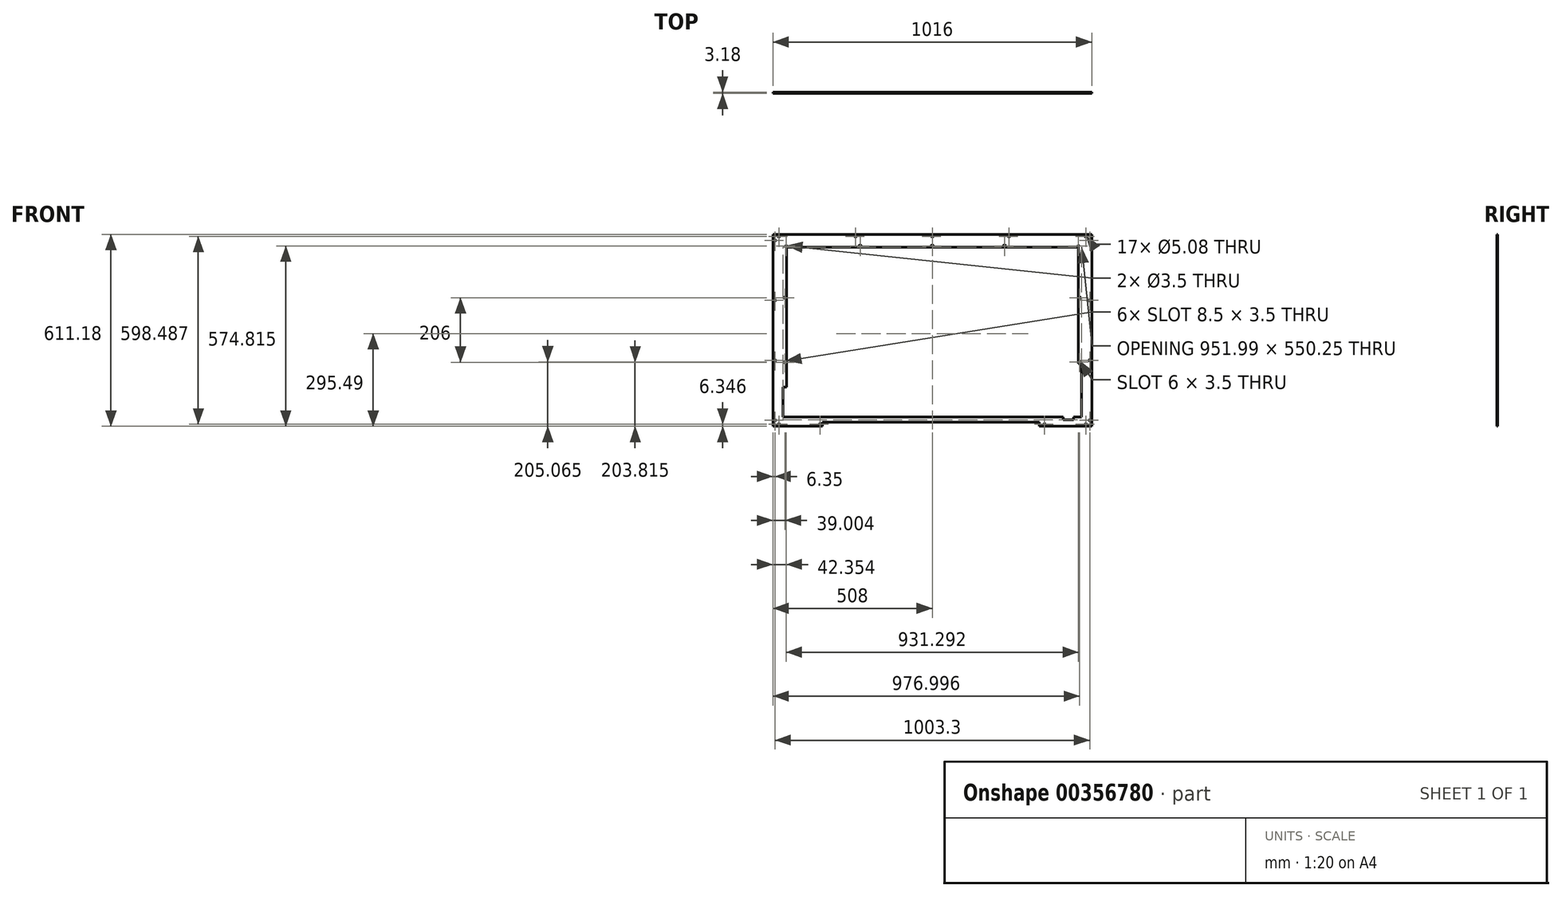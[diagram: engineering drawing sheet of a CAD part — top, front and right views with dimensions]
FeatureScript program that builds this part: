
annotation { "Feature Type Name" : "Feature", "Feature Type Description" : "" }
export const myFeature = defineFeature(function(context is Context, id is Id, definition is map)
    precondition{}
    {
        {
            var Q0;
            Q0=qCreatedBy(makeId("Front.planeOp"),FACE);
            var sketch = newSketch(context, id + "F0", { "sketchPlane" : qUnion([Q0])});
            skLineSegment(sketch, "E0.bottom", {"start": v(495.3, 292.9) * mm, "end": v(-495.3, 292.9) * mm});
            skLineSegment(sketch, "E0.top", {"start": v(495.3, -292.9) * mm, "end": v(-495.3, -292.9) * mm});
            skLineSegment(sketch, "E0.left", {"start": v(495.3, 292.9) * mm, "end": v(495.3, -292.9) * mm});
            skLineSegment(sketch, "E0.right", {"start": v(-495.3, 292.9) * mm, "end": v(-495.3, -292.9) * mm});
            skPoint(sketch, "E0.middle", {"position": v(0, 0) * mm});
            skLineSegment(sketch, "E1.0", {"start": v(-508, 305.6) * mm, "end": v(-508, -305.6) * mm});
            skLineSegment(sketch, "E1.1", {"start": v(508, 305.6) * mm, "end": v(-508, 305.6) * mm});
            skLineSegment(sketch, "E1.2", {"start": v(508, 305.6) * mm, "end": v(508, -305.6) * mm});
            skLineSegment(sketch, "E1.3", {"start": v(508, -305.6) * mm, "end": v(-508, -305.6) * mm});
            skLineSegment(sketch, "E2.bottom", {"start": v(-476, 276.23) * mm, "end": v(476, 276.23) * mm});
            skLineSegment(sketch, "E2.top", {"start": v(-476, -276.23) * mm, "end": v(476, -276.23) * mm});
            skLineSegment(sketch, "E2.left", {"start": v(-476, 276.23) * mm, "end": v(-476, -276.23) * mm});
            skLineSegment(sketch, "E2.right", {"start": v(476, 276.22) * mm, "end": v(476, -276.23) * mm});
            skLineSegment(sketch, "E3", {"start": v(-508, 305.6) * mm, "end": v(-495.3, 292.9) * mm});
            skPoint(sketch, "E4.middle", {"position": v(-501.65, 299.24) * mm});
            skLineSegment(sketch, "E5.bottom", {"start": v(-355.3, -296.7) * mm, "end": v(-360.38, -296.7) * mm});
            skLineSegment(sketch, "E5.top", {"start": v(-355.3, -301.78) * mm, "end": v(-360.38, -301.78) * mm});
            skLineSegment(sketch, "E5.left", {"start": v(-355.3, -296.7) * mm, "end": v(-355.3, -301.78) * mm});
            skLineSegment(sketch, "E5.right", {"start": v(-360.38, -296.7) * mm, "end": v(-360.38, -301.78) * mm});
            skPoint(sketch, "E5.middle", {"position": v(-357.84, -299.24) * mm});
            skLineSegment(sketch, "E6.MirrorCS", {"start": v(360.38, -296.7) * mm, "end": v(360.38, -301.78) * mm});
            skLineSegment(sketch, "E7.MirrorCS", {"start": v(355.3, -296.7) * mm, "end": v(360.38, -296.7) * mm});
            skLineSegment(sketch, "E8.MirrorCS", {"start": v(355.3, -296.7) * mm, "end": v(355.3, -301.78) * mm});
            skLineSegment(sketch, "E9.MirrorCS", {"start": v(355.3, -301.78) * mm, "end": v(360.38, -301.78) * mm});
            skLineSegment(sketch, "E10.bottom", {"start": v(-486.41, 296.7) * mm, "end": v(-491.5, 296.7) * mm});
            skLineSegment(sketch, "E10.top", {"start": v(-486.41, 301.78) * mm, "end": v(-491.5, 301.78) * mm});
            skLineSegment(sketch, "E10.left", {"start": v(-486.41, 296.7) * mm, "end": v(-486.41, 301.78) * mm});
            skLineSegment(sketch, "E10.right", {"start": v(-491.5, 296.7) * mm, "end": v(-491.5, 301.78) * mm});
            skPoint(sketch, "E10.middle", {"position": v(-488.95, 299.24) * mm});
            skLineSegment(sketch, "E11.MirrorCS", {"start": v(-504.19, 284) * mm, "end": v(-504.19, 289.08) * mm});
            skLineSegment(sketch, "E12.MirrorCS", {"start": v(-499.11, 289.08) * mm, "end": v(-504.2, 289.08) * mm});
            skLineSegment(sketch, "E13.MirrorCS", {"start": v(-499.11, 284) * mm, "end": v(-499.11, 289.08) * mm});
            skLineSegment(sketch, "E14.MirrorCS", {"start": v(-499.11, 284) * mm, "end": v(-504.2, 284) * mm});
            skCircle(sketch, "E15", {"center": v(-488.95, 299.24) * mm, "radius": 5.97 * mm});
            skLineSegment(sketch, "E16.MirrorCS", {"start": v(499.11, 284) * mm, "end": v(499.11, 289.08) * mm});
            skLineSegment(sketch, "E17.MirrorCS", {"start": v(499.11, 284) * mm, "end": v(504.2, 284) * mm});
            skLineSegment(sketch, "E18.MirrorCS", {"start": v(499.11, 289.08) * mm, "end": v(504.2, 289.08) * mm});
            skLineSegment(sketch, "E19.MirrorCS", {"start": v(504.19, 284) * mm, "end": v(504.19, 289.08) * mm});
            skLineSegment(sketch, "E20.MirrorCS", {"start": v(486.41, 301.78) * mm, "end": v(491.5, 301.78) * mm});
            skLineSegment(sketch, "E21.MirrorCS", {"start": v(486.41, 296.7) * mm, "end": v(486.41, 301.78) * mm});
            skLineSegment(sketch, "E22.MirrorCS", {"start": v(486.41, 296.7) * mm, "end": v(491.5, 296.7) * mm});
            skLineSegment(sketch, "E23.MirrorCS", {"start": v(491.5, 296.7) * mm, "end": v(491.5, 301.78) * mm});
            skPoint(sketch, "E24.MirrorP", {"position": v(488.95, 299.24) * mm});
            skLineSegment(sketch, "E25.MirrorCS", {"start": v(-499.11, -289.08) * mm, "end": v(-504.2, -289.08) * mm});
            skLineSegment(sketch, "E26.MirrorCS", {"start": v(-499.11, -284) * mm, "end": v(-499.11, -289.08) * mm});
            skLineSegment(sketch, "E27.MirrorCS", {"start": v(-499.11, -284) * mm, "end": v(-504.2, -284) * mm});
            skLineSegment(sketch, "E28.MirrorCS", {"start": v(-504.19, -284) * mm, "end": v(-504.19, -289.08) * mm});
            skLineSegment(sketch, "E29.MirrorCS", {"start": v(-486.41, -301.78) * mm, "end": v(-491.5, -301.78) * mm});
            skLineSegment(sketch, "E30.MirrorCS", {"start": v(-491.5, -296.7) * mm, "end": v(-491.5, -301.78) * mm});
            skPoint(sketch, "E31.MirrorP", {"position": v(-488.95, -299.24) * mm});
            skLineSegment(sketch, "E32.MirrorCS", {"start": v(-486.41, -296.7) * mm, "end": v(-486.41, -301.78) * mm});
            skLineSegment(sketch, "E33.MirrorCS", {"start": v(-486.41, -296.7) * mm, "end": v(-491.5, -296.7) * mm});
            skLineSegment(sketch, "E34.MirrorCS", {"start": v(486.41, -296.7) * mm, "end": v(486.41, -301.78) * mm});
            skPoint(sketch, "E35.MirrorP", {"position": v(488.95, -299.24) * mm});
            skLineSegment(sketch, "E36.MirrorCS", {"start": v(491.5, -296.7) * mm, "end": v(491.5, -301.78) * mm});
            skLineSegment(sketch, "E37.MirrorCS", {"start": v(486.41, -296.7) * mm, "end": v(491.5, -296.7) * mm});
            skLineSegment(sketch, "E38.MirrorCS", {"start": v(486.41, -301.78) * mm, "end": v(491.5, -301.78) * mm});
            skLineSegment(sketch, "E39.MirrorCS", {"start": v(499.11, -289.08) * mm, "end": v(504.2, -289.08) * mm});
            skLineSegment(sketch, "E40.MirrorCS", {"start": v(504.19, -284) * mm, "end": v(504.19, -289.08) * mm});
            skLineSegment(sketch, "E41.MirrorCS", {"start": v(499.11, -284) * mm, "end": v(499.11, -289.08) * mm});
            skLineSegment(sketch, "E42.MirrorCS", {"start": v(499.11, -284) * mm, "end": v(504.2, -284) * mm});
            skLineSegment(sketch, "E43.bottom", {"start": v(-504.19, 92.97) * mm, "end": v(-499.11, 92.97) * mm});
            skLineSegment(sketch, "E43.top", {"start": v(-504.19, 98.05) * mm, "end": v(-499.11, 98.05) * mm});
            skLineSegment(sketch, "E43.left", {"start": v(-504.2, 92.97) * mm, "end": v(-504.2, 98.05) * mm});
            skLineSegment(sketch, "E43.right", {"start": v(-499.11, 92.97) * mm, "end": v(-499.11, 98.05) * mm});
            skPoint(sketch, "E43.middle", {"position": v(-501.65, 95.51) * mm});
            skLineSegment(sketch, "E44.bottom", {"start": v(-499.11, -92.97) * mm, "end": v(-504.19, -92.97) * mm});
            skLineSegment(sketch, "E44.top", {"start": v(-499.11, -98.05) * mm, "end": v(-504.19, -98.05) * mm});
            skLineSegment(sketch, "E44.left", {"start": v(-499.11, -92.97) * mm, "end": v(-499.11, -98.05) * mm});
            skLineSegment(sketch, "E44.right", {"start": v(-504.2, -92.97) * mm, "end": v(-504.2, -98.05) * mm});
            skPoint(sketch, "E44.middle", {"position": v(-501.65, -95.51) * mm});
            skLineSegment(sketch, "E45", {"start": v(-501.65, -284) * mm, "end": v(-501.65, -98.05) * mm});
            skLineSegment(sketch, "E46", {"start": v(-501.65, -92.97) * mm, "end": v(-501.65, 92.97) * mm});
            skLineSegment(sketch, "E47", {"start": v(-501.65, 98.05) * mm, "end": v(-501.65, 284) * mm});
            skLineSegment(sketch, "E48.bottom", {"start": v(2.54, 301.78) * mm, "end": v(-2.54, 301.78) * mm});
            skLineSegment(sketch, "E48.top", {"start": v(2.54, 296.7) * mm, "end": v(-2.54, 296.7) * mm});
            skLineSegment(sketch, "E48.left", {"start": v(2.54, 301.78) * mm, "end": v(2.54, 296.7) * mm});
            skLineSegment(sketch, "E48.right", {"start": v(-2.54, 301.78) * mm, "end": v(-2.54, 296.7) * mm});
            skPoint(sketch, "E48.middle", {"position": v(0, 299.24) * mm});
            skPoint(sketch, "E48.middle.positionSnap0", {"position": v(0, 305.6) * mm});
            skPoint(sketch, "E48.centerSnap0", {"position": v(0, 305.6) * mm});
            skLineSegment(sketch, "E49.bottom", {"start": v(-241.94, 301.78) * mm, "end": v(-247.02, 301.78) * mm});
            skLineSegment(sketch, "E49.top", {"start": v(-241.94, 296.7) * mm, "end": v(-247.02, 296.7) * mm});
            skLineSegment(sketch, "E49.left", {"start": v(-241.94, 301.78) * mm, "end": v(-241.94, 296.7) * mm});
            skLineSegment(sketch, "E49.right", {"start": v(-247.02, 301.78) * mm, "end": v(-247.02, 296.7) * mm});
            skPoint(sketch, "E49.middle", {"position": v(-244.48, 299.24) * mm});
            skLineSegment(sketch, "E50.MirrorCS", {"start": v(241.94, 296.7) * mm, "end": v(247.02, 296.7) * mm});
            skPoint(sketch, "E51.MirrorP", {"position": v(244.48, 299.24) * mm});
            skLineSegment(sketch, "E52.MirrorCS", {"start": v(247.02, 301.78) * mm, "end": v(247.02, 296.7) * mm});
            skLineSegment(sketch, "E53.MirrorCS", {"start": v(241.94, 301.78) * mm, "end": v(247.02, 301.78) * mm});
            skLineSegment(sketch, "E54.MirrorCS", {"start": v(241.94, 301.78) * mm, "end": v(241.94, 296.7) * mm});
            skLineSegment(sketch, "E55.MirrorCS", {"start": v(504.19, 92.97) * mm, "end": v(499.11, 92.97) * mm});
            skLineSegment(sketch, "E56.MirrorCS", {"start": v(499.11, 92.97) * mm, "end": v(499.11, 98.05) * mm});
            skPoint(sketch, "E57.MirrorP", {"position": v(501.65, 95.51) * mm});
            skLineSegment(sketch, "E58.MirrorCS", {"start": v(504.19, 98.05) * mm, "end": v(499.11, 98.05) * mm});
            skLineSegment(sketch, "E59.MirrorCS", {"start": v(504.2, 92.97) * mm, "end": v(504.2, 98.05) * mm});
            skLineSegment(sketch, "E60.MirrorCS", {"start": v(499.11, -98.05) * mm, "end": v(504.19, -98.05) * mm});
            skLineSegment(sketch, "E61.MirrorCS", {"start": v(499.11, -92.97) * mm, "end": v(499.11, -98.05) * mm});
            skLineSegment(sketch, "E62.MirrorCS", {"start": v(499.11, -92.97) * mm, "end": v(504.19, -92.97) * mm});
            skPoint(sketch, "E63.MirrorP", {"position": v(501.65, -95.51) * mm});
            skLineSegment(sketch, "E64.MirrorCS", {"start": v(504.2, -92.97) * mm, "end": v(504.2, -98.05) * mm});
            skLineSegment(sketch, "E65.bottom", {"start": v(-464.8, 265.03) * mm, "end": v(464.8, 265.03) * mm});
            skLineSegment(sketch, "E65.top", {"start": v(-464.8, -265.03) * mm, "end": v(464.8, -265.03) * mm});
            skLineSegment(sketch, "E65.left", {"start": v(-464.8, 265.03) * mm, "end": v(-464.8, -265.03) * mm});
            skLineSegment(sketch, "E65.right", {"start": v(464.8, 265.03) * mm, "end": v(464.8, -265.03) * mm});
            skCircle(sketch, "E66", {"center": v(465.65, 269.23) * mm, "radius": 1.75 * mm});
            skCircle(sketch, "E67", {"center": v(0, 269.23) * mm, "radius": 1.75 * mm});
            skLineSegment(sketch, "E68", {"start": v(0, 269.23) * mm, "end": v(0, 276.23) * mm});
            skLineSegment(sketch, "E69", {"start": v(465.65, 269.23) * mm, "end": v(465.65, 276.23) * mm});
            skCircle(sketch, "E70", {"center": v(230, 269.23) * mm, "radius": 1.75 * mm});
            skLineSegment(sketch, "E71", {"start": v(230, 269.23) * mm, "end": v(230, 276.23) * mm});
            skCircle(sketch, "E72.MirrorC", {"center": v(-230, 269.23) * mm, "radius": 1.75 * mm});
            skCircle(sketch, "E73.MirrorC", {"center": v(-465.65, 269.23) * mm, "radius": 1.75 * mm});
            skCircle(sketch, "E74", {"center": v(469, 104.22) * mm, "radius": 1.75 * mm});
            skCircle(sketch, "E75", {"center": v(469, -101.78) * mm, "radius": 1.75 * mm});
            skLineSegment(sketch, "E76", {"start": v(469, -101.78) * mm, "end": v(476, -101.78) * mm});
            skLineSegment(sketch, "E77", {"start": v(469, 104.22) * mm, "end": v(476, 104.22) * mm});
            skCircle(sketch, "E78.MirrorC", {"center": v(-469, -101.78) * mm, "radius": 1.75 * mm});
            skCircle(sketch, "E79.MirrorC", {"center": v(-469, 104.22) * mm, "radius": 1.75 * mm});
            skLineSegment(sketch, "E80", {"start": v(2.5, 269.23) * mm, "end": v(-2.5, 269.23) * mm});
            skArc(sketch, "E81.0.startCap", {"start": v(2.5, 270.98) * mm, "mid": v(4.25, 269.23) * mm, "end": v(2.5, 267.48) * mm});
            skArc(sketch, "E81.0.endCap", {"start": v(-2.5, 267.48) * mm, "mid": v(-4.25, 269.23) * mm, "end": v(-2.5, 270.98) * mm});
            skLineSegment(sketch, "E81.0.left", {"start": v(2.5, 267.48) * mm, "end": v(-2.5, 267.48) * mm});
            skLineSegment(sketch, "E81.0.right", {"start": v(2.5, 270.98) * mm, "end": v(-2.5, 270.98) * mm});
            skLineSegment(sketch, "E82", {"start": v(232.5, 269.22) * mm, "end": v(227.5, 269.22) * mm});
            skArc(sketch, "E83.0.startCap", {"start": v(232.5, 270.97) * mm, "mid": v(234.25, 269.22) * mm, "end": v(232.5, 267.47) * mm});
            skArc(sketch, "E83.0.endCap", {"start": v(227.5, 267.47) * mm, "mid": v(225.75, 269.22) * mm, "end": v(227.5, 270.97) * mm});
            skLineSegment(sketch, "E83.0.left", {"start": v(232.5, 267.47) * mm, "end": v(227.5, 267.47) * mm});
            skLineSegment(sketch, "E83.0.right", {"start": v(232.5, 270.97) * mm, "end": v(227.5, 270.97) * mm});
            skLineSegment(sketch, "E84.MirrorCS", {"start": v(-232.5, 270.97) * mm, "end": v(-227.5, 270.97) * mm});
            skArc(sketch, "E85.MirrorCS", {"start": v(-227.5, 267.47) * mm, "mid": v(-225.75, 269.22) * mm, "end": v(-227.5, 270.97) * mm});
            skLineSegment(sketch, "E86.MirrorCS", {"start": v(-232.5, 267.47) * mm, "end": v(-227.5, 267.47) * mm});
            skArc(sketch, "E87.MirrorCS", {"start": v(-232.5, 270.97) * mm, "mid": v(-234.25, 269.22) * mm, "end": v(-232.5, 267.47) * mm});
            skLineSegment(sketch, "E88", {"start": v(469, 106.72) * mm, "end": v(469, 101.73) * mm});
            skLineSegment(sketch, "E89", {"start": v(469, -99.28) * mm, "end": v(469, -104.27) * mm});
            skArc(sketch, "E90.0.startCap", {"start": v(467.25, 106.72) * mm, "mid": v(469, 108.47) * mm, "end": v(470.75, 106.72) * mm});
            skArc(sketch, "E90.0.endCap", {"start": v(470.75, 101.73) * mm, "mid": v(469, 99.98) * mm, "end": v(467.25, 101.73) * mm});
            skLineSegment(sketch, "E90.0.left", {"start": v(470.75, 106.72) * mm, "end": v(470.75, 101.73) * mm});
            skLineSegment(sketch, "E90.0.right", {"start": v(467.25, 106.72) * mm, "end": v(467.25, 101.73) * mm});
            skArc(sketch, "E90.1.endCap", {"start": v(467.25, -99.28) * mm, "mid": v(469, -97.53) * mm, "end": v(470.75, -99.28) * mm});
            skLineSegment(sketch, "E91.MirrorCS", {"start": v(-470.75, -99.28) * mm, "end": v(-470.75, -104.27) * mm});
            skArc(sketch, "E92.MirrorCS", {"start": v(-467.25, -99.28) * mm, "mid": v(-469, -97.53) * mm, "end": v(-470.75, -99.28) * mm});
            skLineSegment(sketch, "E93.MirrorCS", {"start": v(-467.25, -99.28) * mm, "end": v(-467.25, -104.27) * mm});
            skArc(sketch, "E94.MirrorCS", {"start": v(-470.75, -104.27) * mm, "mid": v(-469, -106.02) * mm, "end": v(-467.25, -104.27) * mm});
            skLineSegment(sketch, "E95.MirrorCS", {"start": v(-470.75, 106.72) * mm, "end": v(-470.75, 101.73) * mm});
            skArc(sketch, "E96.MirrorCS", {"start": v(-467.25, 106.72) * mm, "mid": v(-469, 108.47) * mm, "end": v(-470.75, 106.72) * mm});
            skLineSegment(sketch, "E97.MirrorCS", {"start": v(-467.25, 106.72) * mm, "end": v(-467.25, 101.73) * mm});
            skArc(sketch, "E98.MirrorCS", {"start": v(-470.75, 101.73) * mm, "mid": v(-469, 99.98) * mm, "end": v(-467.25, 101.73) * mm});
            skPoint(sketch, "E99.centerSnap0", {"position": v(504.19, 286.54) * mm});
            skPoint(sketch, "E99.centerSnap1", {"position": v(501.65, 289.08) * mm});
            skCircle(sketch, "E100", {"center": v(501.65, 286.54) * mm, "radius": 2.54 * mm});
            skPoint(sketch, "E100.centerSnap0", {"position": v(501.65, 284) * mm});
            skCircle(sketch, "E101", {"center": v(488.95, 299.24) * mm, "radius": 2.54 * mm});
            skCircle(sketch, "E102", {"center": v(244.48, 299.24) * mm, "radius": 2.54 * mm});
            skCircle(sketch, "E103", {"center": v(0, 299.24) * mm, "radius": 2.54 * mm});
            skCircle(sketch, "E104", {"center": v(-244.48, 299.24) * mm, "radius": 2.54 * mm});
            skCircle(sketch, "E105", {"center": v(-488.95, 299.24) * mm, "radius": 2.54 * mm});
            skCircle(sketch, "E106", {"center": v(-501.65, 286.54) * mm, "radius": 2.54 * mm});
            skPoint(sketch, "E106.centerSnap0", {"position": v(-504.19, 286.54) * mm});
            skPoint(sketch, "E106.centerSnap1", {"position": v(-501.65, 289.08) * mm});
            skCircle(sketch, "E107", {"center": v(-501.65, 95.51) * mm, "radius": 2.54 * mm});
            skCircle(sketch, "E108", {"center": v(-501.65, -95.51) * mm, "radius": 2.54 * mm});
            skCircle(sketch, "E109", {"center": v(-501.65, -286.54) * mm, "radius": 2.54 * mm});
            skPoint(sketch, "E109.centerSnap0", {"position": v(-504.19, -286.54) * mm});
            skPoint(sketch, "E109.centerSnap1", {"position": v(-501.65, -289.08) * mm});
            skCircle(sketch, "E110", {"center": v(-488.95, -299.24) * mm, "radius": 2.54 * mm});
            skCircle(sketch, "E111", {"center": v(-357.84, -299.24) * mm, "radius": 2.54 * mm});
            skCircle(sketch, "E112", {"center": v(357.84, -299.24) * mm, "radius": 2.54 * mm});
            skPoint(sketch, "E112.centerSnap0", {"position": v(357.84, -301.78) * mm});
            skPoint(sketch, "E112.centerSnap1", {"position": v(355.3, -299.24) * mm});
            skCircle(sketch, "E113", {"center": v(501.65, -286.54) * mm, "radius": 2.54 * mm});
            skPoint(sketch, "E113.centerSnap0", {"position": v(501.65, -284) * mm});
            skPoint(sketch, "E113.centerSnap1", {"position": v(504.19, -286.54) * mm});
            skCircle(sketch, "E114", {"center": v(488.95, -299.24) * mm, "radius": 2.54 * mm});
            skLineSegment(sketch, "E115", {"start": v(476, -105.78) * mm, "end": v(464.8, -105.78) * mm});
            skLineSegment(sketch, "E116", {"start": v(467.25, -99.28) * mm, "end": v(467.25, -101.78) * mm});
            skLineSegment(sketch, "E117", {"start": v(470.75, -99.28) * mm, "end": v(470.75, -101.78) * mm});
            skLineSegment(sketch, "E118", {"start": v(-456.78, -180.78) * mm, "end": v(-484.7, -180.78) * mm});
            skLineSegment(sketch, "E119.bottom", {"start": v(450.6, -276.23) * mm, "end": v(416.6, -276.23) * mm});
            skLineSegment(sketch, "E119.top", {"start": v(450.6, -285.23) * mm, "end": v(416.6, -285.23) * mm});
            skLineSegment(sketch, "E119.left", {"start": v(450.6, -276.23) * mm, "end": v(450.6, -285.23) * mm});
            skLineSegment(sketch, "E119.right", {"start": v(416.6, -276.23) * mm, "end": v(416.6, -285.23) * mm});
            skCircle(sketch, "E120", {"center": v(501.65, -95.51) * mm, "radius": 2.54 * mm});
            skCircle(sketch, "E121", {"center": v(501.65, 95.51) * mm, "radius": 2.54 * mm});
            skLineSegment(sketch, "E122", {"start": v(340.3, -288.4) * mm, "end": v(340.3, -317.05) * mm});
            skLineSegment(sketch, "E123", {"start": v(-350.3, -282.76) * mm, "end": v(-350.3, -322.45) * mm});
            skSolve(sketch);
        }
        {
            var Q0;
            {var subQ3=sQuery(id+"F0.wireOp",EDGE,"E0.left");Q0=makeQuery(id+"F0.imprint","IMPRINT",FACE,{"disambiguationData":[TD([[makeQuery(id+"F0.imprint","IMPRINT",EDGE,{"derivedFrom":subQ3}),-1.0]])]});}
            var Q1;
            {var subQ9=sQuery(id+"F0.wireOp",EDGE,"E0.left");Q1=makeQuery(id+"F0.imprint","IMPRINT",FACE,{"disambiguationData":[TD([[makeQuery(id+"F0.imprint","IMPRINT",EDGE,{"derivedFrom":subQ9}),1.0]])]});}
            var Q2;
            {var subQ1=sQuery(id+"F0.wireOp",EDGE,"O24vq0J8-WJNd-eW1m-mhOj-HjlkgafQAecY.top");Q2=makeQuery(id+"F0.imprint","IMPRINT",FACE,{"disambiguationData":[TD([[makeQuery(id+"F0.imprint","IMPRINT",EDGE,{"derivedFrom":subQ1}),1.0]])]});}
            var Q3;
            {var subQ9=sQuery(id+"F0.wireOp",EDGE,"O24vq0J8-WJNd-eW1m-mhOj-HjlkgafQAecY.bottom");Q3=makeQuery(id+"F0.imprint","IMPRINT",FACE,{"disambiguationData":[TD([[makeQuery(id+"F0.imprint","IMPRINT",EDGE,{"derivedFrom":subQ9}),-1.0]])]});}
            var Q4;
            {var subQ5=sQuery(id+"F0.wireOp",EDGE,"E0.right");Q4=makeQuery(id+"F0.imprint","IMPRINT",FACE,{"disambiguationData":[TD([[makeQuery(id+"F0.imprint","IMPRINT",EDGE,{"derivedFrom":subQ5}),-1.0]])]});}
            var Q5;
            {var subQ5=sQuery(id+"F0.wireOp",EDGE,"E4.bottom");Q5=makeQuery(id+"F0.imprint","IMPRINT",FACE,{"disambiguationData":[TD([[makeQuery(id+"F0.imprint","IMPRINT",EDGE,{"derivedFrom":subQ5}),-1.0]])]});}
            var Q6;
            {var subQ7=sQuery(id+"F0.wireOp",EDGE,"E4.right");Q6=makeQuery(id+"F0.imprint","IMPRINT",FACE,{"disambiguationData":[TD([[makeQuery(id+"F0.imprint","IMPRINT",EDGE,{"derivedFrom":subQ7}),-1.0]])]});}
            var Q7;
            {var subQ3=sQuery(id+"F0.wireOp",EDGE,"0pr6R6qP-uFYV-tloq-gIhA-llGfv03A3eT7");var subQ5=sQuery(id+"F0.wireOp",EDGE,"hnryXjpA-dOW9-xkJg-QQz7-FwJbjo40cldU");var subQ6=makeQuery(id+"F0.imprint","INTERSECT",VERTEX,{"derivedFrom":[subQ3,subQ5]});Q7=makeQuery(id+"F0.imprint","IMPRINT",FACE,{"disambiguationData":[TD([[makeQuery(id+"F0.imprint","IMPRINT",EDGE,{"disambiguationData":[TD([[subQ6,-1.0]])],"derivedFrom":subQ3}),1.0]])]});}
            var Q8;
            {var subQ1=sQuery(id+"F0.wireOp",EDGE,"E3");var subQ3=sQuery(id+"F0.wireOp",EDGE,"0pr6R6qP-uFYV-tloq-gIhA-llGfv03A3eT7");var subQ4=makeQuery(id+"F0.imprint","INTERSECT",VERTEX,{"disambiguationData":[OD(1.0)],"derivedFrom":[subQ1,subQ3]});Q8=makeQuery(id+"F0.imprint","IMPRINT",FACE,{"disambiguationData":[TD([[makeQuery(id+"F0.imprint","IMPRINT",EDGE,{"disambiguationData":[TD([[subQ4,-1.0]])],"derivedFrom":subQ3}),1.0]])]});}
            var Q9;
            Q9=makeQuery(id+"F0.imprint","IMPRINT",FACE,{"disambiguationData":[TD([[makeQuery(id+"F0.imprint","IMPRINT",EDGE,{"derivedFrom":sQuery(id+"F0.wireOp",EDGE,"E2.bottom")}),-1.0]])]});
            var Q10;
            Q10=makeQuery(id+"F0.imprint","IMPRINT",FACE,{"disambiguationData":[TD([[makeQuery(id+"F0.imprint","IMPRINT",EDGE,{"derivedFrom":sQuery(id+"F0.wireOp",EDGE,"E10.bottom")}),1.0]])]});
            var Q11;
            {var subQ0=sQuery(id+"F0.wireOp",EDGE,"E22.MirrorCS");var subQ1=sQuery(id+"F0.wireOp",EDGE,"E21.MirrorCS");var subQ2=makeQuery(id+"F0.imprint","INTERSECT",VERTEX,{"derivedFrom":[subQ1,subQ0]});Q11=makeQuery(id+"F0.imprint","IMPRINT",FACE,{"disambiguationData":[TD([[makeQuery(id+"F0.imprint","IMPRINT",EDGE,{"disambiguationData":[TD([[subQ2,-1.0]])],"derivedFrom":subQ1}),-1.0]])]});}
            var Q12;
            {var subQ0=sQuery(id+"F0.wireOp",EDGE,"E21.MirrorCS");var subQ1=sQuery(id+"F0.wireOp",EDGE,"E20.MirrorCS");var subQ2=makeQuery(id+"F0.imprint","INTERSECT",VERTEX,{"derivedFrom":[subQ1,subQ0]});Q12=makeQuery(id+"F0.imprint","IMPRINT",FACE,{"disambiguationData":[TD([[makeQuery(id+"F0.imprint","IMPRINT",EDGE,{"disambiguationData":[TD([[subQ2,-1.0]])],"derivedFrom":subQ1}),-1.0]])]});}
            var Q13;
            {var subQ0=sQuery(id+"F0.wireOp",EDGE,"E23.MirrorCS");var subQ1=sQuery(id+"F0.wireOp",EDGE,"E20.MirrorCS");var subQ2=makeQuery(id+"F0.imprint","INTERSECT",VERTEX,{"derivedFrom":[subQ1,subQ0]});Q13=makeQuery(id+"F0.imprint","IMPRINT",FACE,{"disambiguationData":[TD([[makeQuery(id+"F0.imprint","IMPRINT",EDGE,{"disambiguationData":[TD([[subQ2,1.0]])],"derivedFrom":subQ1}),-1.0]])]});}
            var Q14;
            {var subQ0=sQuery(id+"F0.wireOp",EDGE,"E23.MirrorCS");var subQ1=sQuery(id+"F0.wireOp",EDGE,"E22.MirrorCS");var subQ2=makeQuery(id+"F0.imprint","INTERSECT",VERTEX,{"derivedFrom":[subQ1,subQ0]});Q14=makeQuery(id+"F0.imprint","IMPRINT",FACE,{"disambiguationData":[TD([[makeQuery(id+"F0.imprint","IMPRINT",EDGE,{"disambiguationData":[TD([[subQ2,1.0]])],"derivedFrom":subQ1}),1.0]])]});}
            var Q15;
            {var subQ0=sQuery(id+"F0.wireOp",EDGE,"E18.MirrorCS");var subQ1=sQuery(id+"F0.wireOp",EDGE,"E16.MirrorCS");var subQ2=makeQuery(id+"F0.imprint","INTERSECT",VERTEX,{"derivedFrom":[subQ1,subQ0]});Q15=makeQuery(id+"F0.imprint","IMPRINT",FACE,{"disambiguationData":[TD([[makeQuery(id+"F0.imprint","IMPRINT",EDGE,{"disambiguationData":[TD([[subQ2,1.0]])],"derivedFrom":subQ1}),-1.0]])]});}
            var Q16;
            {var subQ0=sQuery(id+"F0.wireOp",EDGE,"E19.MirrorCS");var subQ1=sQuery(id+"F0.wireOp",EDGE,"E18.MirrorCS");var subQ2=makeQuery(id+"F0.imprint","INTERSECT",VERTEX,{"derivedFrom":[subQ1,subQ0]});Q16=makeQuery(id+"F0.imprint","IMPRINT",FACE,{"disambiguationData":[TD([[makeQuery(id+"F0.imprint","IMPRINT",EDGE,{"disambiguationData":[TD([[subQ2,1.0]])],"derivedFrom":subQ1}),-1.0]])]});}
            var Q17;
            {var subQ0=sQuery(id+"F0.wireOp",EDGE,"E19.MirrorCS");var subQ1=sQuery(id+"F0.wireOp",EDGE,"E17.MirrorCS");var subQ2=makeQuery(id+"F0.imprint","INTERSECT",VERTEX,{"derivedFrom":[subQ1,subQ0]});Q17=makeQuery(id+"F0.imprint","IMPRINT",FACE,{"disambiguationData":[TD([[makeQuery(id+"F0.imprint","IMPRINT",EDGE,{"disambiguationData":[TD([[subQ2,1.0]])],"derivedFrom":subQ1}),1.0]])]});}
            var Q18;
            {var subQ0=sQuery(id+"F0.wireOp",EDGE,"E17.MirrorCS");var subQ1=sQuery(id+"F0.wireOp",EDGE,"E16.MirrorCS");var subQ2=makeQuery(id+"F0.imprint","INTERSECT",VERTEX,{"derivedFrom":[subQ1,subQ0]});Q18=makeQuery(id+"F0.imprint","IMPRINT",FACE,{"disambiguationData":[TD([[makeQuery(id+"F0.imprint","IMPRINT",EDGE,{"disambiguationData":[TD([[subQ2,-1.0]])],"derivedFrom":subQ1}),-1.0]])]});}
            var Q19;
            {var subQ0=sQuery(id+"F0.wireOp",EDGE,"E53.MirrorCS");var subQ1=sQuery(id+"F0.wireOp",EDGE,"E52.MirrorCS");var subQ2=makeQuery(id+"F0.imprint","INTERSECT",VERTEX,{"derivedFrom":[subQ1,subQ0]});Q19=makeQuery(id+"F0.imprint","IMPRINT",FACE,{"disambiguationData":[TD([[makeQuery(id+"F0.imprint","IMPRINT",EDGE,{"disambiguationData":[TD([[subQ2,-1.0]])],"derivedFrom":subQ1}),-1.0]])]});}
            var Q20;
            {var subQ0=sQuery(id+"F0.wireOp",EDGE,"E54.MirrorCS");var subQ1=sQuery(id+"F0.wireOp",EDGE,"E53.MirrorCS");var subQ2=makeQuery(id+"F0.imprint","INTERSECT",VERTEX,{"derivedFrom":[subQ1,subQ0]});Q20=makeQuery(id+"F0.imprint","IMPRINT",FACE,{"disambiguationData":[TD([[makeQuery(id+"F0.imprint","IMPRINT",EDGE,{"disambiguationData":[TD([[subQ2,-1.0]])],"derivedFrom":subQ1}),-1.0]])]});}
            var Q21;
            {var subQ0=sQuery(id+"F0.wireOp",EDGE,"E54.MirrorCS");var subQ1=sQuery(id+"F0.wireOp",EDGE,"E50.MirrorCS");var subQ2=makeQuery(id+"F0.imprint","INTERSECT",VERTEX,{"derivedFrom":[subQ1,subQ0]});Q21=makeQuery(id+"F0.imprint","IMPRINT",FACE,{"disambiguationData":[TD([[makeQuery(id+"F0.imprint","IMPRINT",EDGE,{"disambiguationData":[TD([[subQ2,-1.0]])],"derivedFrom":subQ1}),1.0]])]});}
            var Q22;
            {var subQ0=sQuery(id+"F0.wireOp",EDGE,"E52.MirrorCS");var subQ1=sQuery(id+"F0.wireOp",EDGE,"E50.MirrorCS");var subQ2=makeQuery(id+"F0.imprint","INTERSECT",VERTEX,{"derivedFrom":[subQ1,subQ0]});Q22=makeQuery(id+"F0.imprint","IMPRINT",FACE,{"disambiguationData":[TD([[makeQuery(id+"F0.imprint","IMPRINT",EDGE,{"disambiguationData":[TD([[subQ2,1.0]])],"derivedFrom":subQ1}),1.0]])]});}
            var Q23;
            {var subQ0=sQuery(id+"F0.wireOp",EDGE,"E48.right");var subQ1=sQuery(id+"F0.wireOp",EDGE,"E48.bottom");var subQ2=makeQuery(id+"F0.imprint","INTERSECT",VERTEX,{"derivedFrom":[subQ1,subQ0]});Q23=makeQuery(id+"F0.imprint","IMPRINT",FACE,{"disambiguationData":[TD([[makeQuery(id+"F0.imprint","IMPRINT",EDGE,{"disambiguationData":[TD([[subQ2,1.0]])],"derivedFrom":subQ1}),1.0]])]});}
            var Q24;
            {var subQ0=sQuery(id+"F0.wireOp",EDGE,"E48.right");var subQ1=sQuery(id+"F0.wireOp",EDGE,"E48.top");var subQ2=makeQuery(id+"F0.imprint","INTERSECT",VERTEX,{"derivedFrom":[subQ1,subQ0]});Q24=makeQuery(id+"F0.imprint","IMPRINT",FACE,{"disambiguationData":[TD([[makeQuery(id+"F0.imprint","IMPRINT",EDGE,{"disambiguationData":[TD([[subQ2,1.0]])],"derivedFrom":subQ1}),-1.0]])]});}
            var Q25;
            {var subQ0=sQuery(id+"F0.wireOp",EDGE,"E48.left");var subQ1=sQuery(id+"F0.wireOp",EDGE,"E48.top");var subQ2=makeQuery(id+"F0.imprint","INTERSECT",VERTEX,{"derivedFrom":[subQ1,subQ0]});Q25=makeQuery(id+"F0.imprint","IMPRINT",FACE,{"disambiguationData":[TD([[makeQuery(id+"F0.imprint","IMPRINT",EDGE,{"disambiguationData":[TD([[subQ2,-1.0]])],"derivedFrom":subQ1}),-1.0]])]});}
            var Q26;
            {var subQ0=sQuery(id+"F0.wireOp",EDGE,"E48.left");var subQ1=sQuery(id+"F0.wireOp",EDGE,"E48.bottom");var subQ2=makeQuery(id+"F0.imprint","INTERSECT",VERTEX,{"derivedFrom":[subQ1,subQ0]});Q26=makeQuery(id+"F0.imprint","IMPRINT",FACE,{"disambiguationData":[TD([[makeQuery(id+"F0.imprint","IMPRINT",EDGE,{"disambiguationData":[TD([[subQ2,-1.0]])],"derivedFrom":subQ1}),1.0]])]});}
            var Q27;
            {var subQ0=sQuery(id+"F0.wireOp",EDGE,"E49.left");var subQ1=sQuery(id+"F0.wireOp",EDGE,"E49.bottom");var subQ2=makeQuery(id+"F0.imprint","INTERSECT",VERTEX,{"derivedFrom":[subQ1,subQ0]});Q27=makeQuery(id+"F0.imprint","IMPRINT",FACE,{"disambiguationData":[TD([[makeQuery(id+"F0.imprint","IMPRINT",EDGE,{"disambiguationData":[TD([[subQ2,-1.0]])],"derivedFrom":subQ1}),1.0]])]});}
            var Q28;
            {var subQ0=sQuery(id+"F0.wireOp",EDGE,"E49.right");var subQ1=sQuery(id+"F0.wireOp",EDGE,"E49.bottom");var subQ2=makeQuery(id+"F0.imprint","INTERSECT",VERTEX,{"derivedFrom":[subQ1,subQ0]});Q28=makeQuery(id+"F0.imprint","IMPRINT",FACE,{"disambiguationData":[TD([[makeQuery(id+"F0.imprint","IMPRINT",EDGE,{"disambiguationData":[TD([[subQ2,1.0]])],"derivedFrom":subQ1}),1.0]])]});}
            var Q29;
            {var subQ0=sQuery(id+"F0.wireOp",EDGE,"E49.right");var subQ1=sQuery(id+"F0.wireOp",EDGE,"E49.top");var subQ2=makeQuery(id+"F0.imprint","INTERSECT",VERTEX,{"derivedFrom":[subQ1,subQ0]});Q29=makeQuery(id+"F0.imprint","IMPRINT",FACE,{"disambiguationData":[TD([[makeQuery(id+"F0.imprint","IMPRINT",EDGE,{"disambiguationData":[TD([[subQ2,1.0]])],"derivedFrom":subQ1}),-1.0]])]});}
            var Q30;
            {var subQ0=sQuery(id+"F0.wireOp",EDGE,"E49.left");var subQ1=sQuery(id+"F0.wireOp",EDGE,"E49.top");var subQ2=makeQuery(id+"F0.imprint","INTERSECT",VERTEX,{"derivedFrom":[subQ1,subQ0]});Q30=makeQuery(id+"F0.imprint","IMPRINT",FACE,{"disambiguationData":[TD([[makeQuery(id+"F0.imprint","IMPRINT",EDGE,{"disambiguationData":[TD([[subQ2,-1.0]])],"derivedFrom":subQ1}),-1.0]])]});}
            var Q31;
            {var subQ0=sQuery(id+"F0.wireOp",EDGE,"E10.right");var subQ1=sQuery(id+"F0.wireOp",EDGE,"E10.top");var subQ2=makeQuery(id+"F0.imprint","INTERSECT",VERTEX,{"derivedFrom":[subQ1,subQ0]});Q31=makeQuery(id+"F0.imprint","IMPRINT",FACE,{"disambiguationData":[TD([[makeQuery(id+"F0.imprint","IMPRINT",EDGE,{"disambiguationData":[TD([[subQ2,1.0]])],"derivedFrom":subQ1}),1.0]])]});}
            var Q32;
            {var subQ0=sQuery(id+"F0.wireOp",EDGE,"E10.left");var subQ1=sQuery(id+"F0.wireOp",EDGE,"E10.top");var subQ2=makeQuery(id+"F0.imprint","INTERSECT",VERTEX,{"derivedFrom":[subQ1,subQ0]});Q32=makeQuery(id+"F0.imprint","IMPRINT",FACE,{"disambiguationData":[TD([[makeQuery(id+"F0.imprint","IMPRINT",EDGE,{"disambiguationData":[TD([[subQ2,-1.0]])],"derivedFrom":subQ1}),1.0]])]});}
            var Q33;
            {var subQ0=sQuery(id+"F0.wireOp",EDGE,"E10.left");var subQ1=sQuery(id+"F0.wireOp",EDGE,"E10.bottom");var subQ2=makeQuery(id+"F0.imprint","INTERSECT",VERTEX,{"derivedFrom":[subQ1,subQ0]});Q33=makeQuery(id+"F0.imprint","IMPRINT",FACE,{"disambiguationData":[TD([[makeQuery(id+"F0.imprint","IMPRINT",EDGE,{"disambiguationData":[TD([[subQ2,-1.0]])],"derivedFrom":subQ1}),-1.0]])]});}
            var Q34;
            {var subQ0=sQuery(id+"F0.wireOp",EDGE,"E10.right");var subQ1=sQuery(id+"F0.wireOp",EDGE,"E10.bottom");var subQ2=makeQuery(id+"F0.imprint","INTERSECT",VERTEX,{"derivedFrom":[subQ1,subQ0]});Q34=makeQuery(id+"F0.imprint","IMPRINT",FACE,{"disambiguationData":[TD([[makeQuery(id+"F0.imprint","IMPRINT",EDGE,{"disambiguationData":[TD([[subQ2,1.0]])],"derivedFrom":subQ1}),-1.0]])]});}
            var Q35;
            {var subQ0=sQuery(id+"F0.wireOp",EDGE,"E13.MirrorCS");var subQ1=sQuery(id+"F0.wireOp",EDGE,"E12.MirrorCS");var subQ2=makeQuery(id+"F0.imprint","INTERSECT",VERTEX,{"derivedFrom":[subQ1,subQ0]});Q35=makeQuery(id+"F0.imprint","IMPRINT",FACE,{"disambiguationData":[TD([[makeQuery(id+"F0.imprint","IMPRINT",EDGE,{"disambiguationData":[TD([[subQ2,-1.0]])],"derivedFrom":subQ1}),1.0]])]});}
            var Q36;
            {var subQ0=sQuery(id+"F0.wireOp",EDGE,"E12.MirrorCS");var subQ1=sQuery(id+"F0.wireOp",EDGE,"E11.MirrorCS");var subQ2=makeQuery(id+"F0.imprint","INTERSECT",VERTEX,{"derivedFrom":[subQ1,subQ0]});Q36=makeQuery(id+"F0.imprint","IMPRINT",FACE,{"disambiguationData":[TD([[makeQuery(id+"F0.imprint","IMPRINT",EDGE,{"disambiguationData":[TD([[subQ2,1.0]])],"derivedFrom":subQ1}),-1.0]])]});}
            var Q37;
            {var subQ0=sQuery(id+"F0.wireOp",EDGE,"E14.MirrorCS");var subQ1=sQuery(id+"F0.wireOp",EDGE,"E11.MirrorCS");var subQ2=makeQuery(id+"F0.imprint","INTERSECT",VERTEX,{"derivedFrom":[subQ1,subQ0]});Q37=makeQuery(id+"F0.imprint","IMPRINT",FACE,{"disambiguationData":[TD([[makeQuery(id+"F0.imprint","IMPRINT",EDGE,{"disambiguationData":[TD([[subQ2,-1.0]])],"derivedFrom":subQ1}),-1.0]])]});}
            var Q38;
            {var subQ0=sQuery(id+"F0.wireOp",EDGE,"E14.MirrorCS");var subQ1=sQuery(id+"F0.wireOp",EDGE,"E13.MirrorCS");var subQ2=makeQuery(id+"F0.imprint","INTERSECT",VERTEX,{"derivedFrom":[subQ1,subQ0]});Q38=makeQuery(id+"F0.imprint","IMPRINT",FACE,{"disambiguationData":[TD([[makeQuery(id+"F0.imprint","IMPRINT",EDGE,{"disambiguationData":[TD([[subQ2,-1.0]])],"derivedFrom":subQ1}),1.0]])]});}
            var Q39;
            {var subQ0=sQuery(id+"F0.wireOp",EDGE,"E43.right");var subQ1=sQuery(id+"F0.wireOp",EDGE,"E43.top");var subQ2=makeQuery(id+"F0.imprint","INTERSECT",VERTEX,{"derivedFrom":[subQ1,subQ0]});Q39=makeQuery(id+"F0.imprint","IMPRINT",FACE,{"disambiguationData":[TD([[makeQuery(id+"F0.imprint","IMPRINT",EDGE,{"disambiguationData":[TD([[subQ2,1.0]])],"derivedFrom":subQ1}),-1.0]])]});}
            var Q40;
            {var subQ0=sQuery(id+"F0.wireOp",EDGE,"E43.left");var subQ1=sQuery(id+"F0.wireOp",EDGE,"E43.top");var subQ2=makeQuery(id+"F0.imprint","INTERSECT",VERTEX,{"derivedFrom":[subQ1,subQ0]});Q40=makeQuery(id+"F0.imprint","IMPRINT",FACE,{"disambiguationData":[TD([[makeQuery(id+"F0.imprint","IMPRINT",EDGE,{"disambiguationData":[TD([[subQ2,-1.0]])],"derivedFrom":subQ1}),-1.0]])]});}
            var Q41;
            {var subQ0=sQuery(id+"F0.wireOp",EDGE,"E43.right");var subQ1=sQuery(id+"F0.wireOp",EDGE,"E43.bottom");var subQ2=makeQuery(id+"F0.imprint","INTERSECT",VERTEX,{"derivedFrom":[subQ1,subQ0]});Q41=makeQuery(id+"F0.imprint","IMPRINT",FACE,{"disambiguationData":[TD([[makeQuery(id+"F0.imprint","IMPRINT",EDGE,{"disambiguationData":[TD([[subQ2,1.0]])],"derivedFrom":subQ1}),1.0]])]});}
            var Q42;
            {var subQ0=sQuery(id+"F0.wireOp",EDGE,"E43.left");var subQ1=sQuery(id+"F0.wireOp",EDGE,"E43.bottom");var subQ2=makeQuery(id+"F0.imprint","INTERSECT",VERTEX,{"derivedFrom":[subQ1,subQ0]});Q42=makeQuery(id+"F0.imprint","IMPRINT",FACE,{"disambiguationData":[TD([[makeQuery(id+"F0.imprint","IMPRINT",EDGE,{"disambiguationData":[TD([[subQ2,-1.0]])],"derivedFrom":subQ1}),1.0]])]});}
            var Q43;
            {var subQ0=sQuery(id+"F0.wireOp",EDGE,"E44.left");var subQ1=sQuery(id+"F0.wireOp",EDGE,"E44.bottom");var subQ2=makeQuery(id+"F0.imprint","INTERSECT",VERTEX,{"derivedFrom":[subQ1,subQ0]});Q43=makeQuery(id+"F0.imprint","IMPRINT",FACE,{"disambiguationData":[TD([[makeQuery(id+"F0.imprint","IMPRINT",EDGE,{"disambiguationData":[TD([[subQ2,-1.0]])],"derivedFrom":subQ1}),1.0]])]});}
            var Q44;
            {var subQ0=sQuery(id+"F0.wireOp",EDGE,"E44.right");var subQ1=sQuery(id+"F0.wireOp",EDGE,"E44.bottom");var subQ2=makeQuery(id+"F0.imprint","INTERSECT",VERTEX,{"derivedFrom":[subQ1,subQ0]});Q44=makeQuery(id+"F0.imprint","IMPRINT",FACE,{"disambiguationData":[TD([[makeQuery(id+"F0.imprint","IMPRINT",EDGE,{"disambiguationData":[TD([[subQ2,1.0]])],"derivedFrom":subQ1}),1.0]])]});}
            var Q45;
            {var subQ0=sQuery(id+"F0.wireOp",EDGE,"E44.left");var subQ1=sQuery(id+"F0.wireOp",EDGE,"E44.top");var subQ2=makeQuery(id+"F0.imprint","INTERSECT",VERTEX,{"derivedFrom":[subQ1,subQ0]});Q45=makeQuery(id+"F0.imprint","IMPRINT",FACE,{"disambiguationData":[TD([[makeQuery(id+"F0.imprint","IMPRINT",EDGE,{"disambiguationData":[TD([[subQ2,-1.0]])],"derivedFrom":subQ1}),-1.0]])]});}
            var Q46;
            {var subQ0=sQuery(id+"F0.wireOp",EDGE,"E44.right");var subQ1=sQuery(id+"F0.wireOp",EDGE,"E44.top");var subQ2=makeQuery(id+"F0.imprint","INTERSECT",VERTEX,{"derivedFrom":[subQ1,subQ0]});Q46=makeQuery(id+"F0.imprint","IMPRINT",FACE,{"disambiguationData":[TD([[makeQuery(id+"F0.imprint","IMPRINT",EDGE,{"disambiguationData":[TD([[subQ2,1.0]])],"derivedFrom":subQ1}),-1.0]])]});}
            var Q47;
            {var subQ0=sQuery(id+"F0.wireOp",EDGE,"E27.MirrorCS");var subQ1=sQuery(id+"F0.wireOp",EDGE,"E26.MirrorCS");var subQ2=makeQuery(id+"F0.imprint","INTERSECT",VERTEX,{"derivedFrom":[subQ1,subQ0]});Q47=makeQuery(id+"F0.imprint","IMPRINT",FACE,{"disambiguationData":[TD([[makeQuery(id+"F0.imprint","IMPRINT",EDGE,{"disambiguationData":[TD([[subQ2,-1.0]])],"derivedFrom":subQ1}),-1.0]])]});}
            var Q48;
            {var subQ0=sQuery(id+"F0.wireOp",EDGE,"E28.MirrorCS");var subQ1=sQuery(id+"F0.wireOp",EDGE,"E27.MirrorCS");var subQ2=makeQuery(id+"F0.imprint","INTERSECT",VERTEX,{"derivedFrom":[subQ1,subQ0]});Q48=makeQuery(id+"F0.imprint","IMPRINT",FACE,{"disambiguationData":[TD([[makeQuery(id+"F0.imprint","IMPRINT",EDGE,{"disambiguationData":[TD([[subQ2,1.0]])],"derivedFrom":subQ1}),1.0]])]});}
            var Q49;
            {var subQ0=sQuery(id+"F0.wireOp",EDGE,"E28.MirrorCS");var subQ1=sQuery(id+"F0.wireOp",EDGE,"E25.MirrorCS");var subQ2=makeQuery(id+"F0.imprint","INTERSECT",VERTEX,{"derivedFrom":[subQ1,subQ0]});Q49=makeQuery(id+"F0.imprint","IMPRINT",FACE,{"disambiguationData":[TD([[makeQuery(id+"F0.imprint","IMPRINT",EDGE,{"disambiguationData":[TD([[subQ2,1.0]])],"derivedFrom":subQ1}),-1.0]])]});}
            var Q50;
            {var subQ0=sQuery(id+"F0.wireOp",EDGE,"E26.MirrorCS");var subQ1=sQuery(id+"F0.wireOp",EDGE,"E25.MirrorCS");var subQ2=makeQuery(id+"F0.imprint","INTERSECT",VERTEX,{"derivedFrom":[subQ1,subQ0]});Q50=makeQuery(id+"F0.imprint","IMPRINT",FACE,{"disambiguationData":[TD([[makeQuery(id+"F0.imprint","IMPRINT",EDGE,{"disambiguationData":[TD([[subQ2,-1.0]])],"derivedFrom":subQ1}),-1.0]])]});}
            var Q51;
            {var subQ0=sQuery(id+"F0.wireOp",EDGE,"E33.MirrorCS");var subQ1=sQuery(id+"F0.wireOp",EDGE,"E30.MirrorCS");var subQ2=makeQuery(id+"F0.imprint","INTERSECT",VERTEX,{"derivedFrom":[subQ1,subQ0]});Q51=makeQuery(id+"F0.imprint","IMPRINT",FACE,{"disambiguationData":[TD([[makeQuery(id+"F0.imprint","IMPRINT",EDGE,{"disambiguationData":[TD([[subQ2,-1.0]])],"derivedFrom":subQ1}),1.0]])]});}
            var Q52;
            {var subQ0=sQuery(id+"F0.wireOp",EDGE,"E33.MirrorCS");var subQ1=sQuery(id+"F0.wireOp",EDGE,"E32.MirrorCS");var subQ2=makeQuery(id+"F0.imprint","INTERSECT",VERTEX,{"derivedFrom":[subQ1,subQ0]});Q52=makeQuery(id+"F0.imprint","IMPRINT",FACE,{"disambiguationData":[TD([[makeQuery(id+"F0.imprint","IMPRINT",EDGE,{"disambiguationData":[TD([[subQ2,-1.0]])],"derivedFrom":subQ1}),-1.0]])]});}
            var Q53;
            {var subQ0=sQuery(id+"F0.wireOp",EDGE,"E32.MirrorCS");var subQ1=sQuery(id+"F0.wireOp",EDGE,"E29.MirrorCS");var subQ2=makeQuery(id+"F0.imprint","INTERSECT",VERTEX,{"derivedFrom":[subQ1,subQ0]});Q53=makeQuery(id+"F0.imprint","IMPRINT",FACE,{"disambiguationData":[TD([[makeQuery(id+"F0.imprint","IMPRINT",EDGE,{"disambiguationData":[TD([[subQ2,-1.0]])],"derivedFrom":subQ1}),-1.0]])]});}
            var Q54;
            {var subQ0=sQuery(id+"F0.wireOp",EDGE,"E30.MirrorCS");var subQ1=sQuery(id+"F0.wireOp",EDGE,"E29.MirrorCS");var subQ2=makeQuery(id+"F0.imprint","INTERSECT",VERTEX,{"derivedFrom":[subQ1,subQ0]});Q54=makeQuery(id+"F0.imprint","IMPRINT",FACE,{"disambiguationData":[TD([[makeQuery(id+"F0.imprint","IMPRINT",EDGE,{"disambiguationData":[TD([[subQ2,1.0]])],"derivedFrom":subQ1}),-1.0]])]});}
            var Q55;
            {var subQ0=sQuery(id+"F0.wireOp",EDGE,"E5.left");var subQ1=sQuery(id+"F0.wireOp",EDGE,"E5.bottom");var subQ2=makeQuery(id+"F0.imprint","INTERSECT",VERTEX,{"derivedFrom":[subQ1,subQ0]});Q55=makeQuery(id+"F0.imprint","IMPRINT",FACE,{"disambiguationData":[TD([[makeQuery(id+"F0.imprint","IMPRINT",EDGE,{"disambiguationData":[TD([[subQ2,-1.0]])],"derivedFrom":subQ1}),1.0]])]});}
            var Q56;
            {var subQ0=sQuery(id+"F0.wireOp",EDGE,"E5.right");var subQ1=sQuery(id+"F0.wireOp",EDGE,"E5.bottom");var subQ2=makeQuery(id+"F0.imprint","INTERSECT",VERTEX,{"derivedFrom":[subQ1,subQ0]});Q56=makeQuery(id+"F0.imprint","IMPRINT",FACE,{"disambiguationData":[TD([[makeQuery(id+"F0.imprint","IMPRINT",EDGE,{"disambiguationData":[TD([[subQ2,1.0]])],"derivedFrom":subQ1}),1.0]])]});}
            var Q57;
            {var subQ0=sQuery(id+"F0.wireOp",EDGE,"E5.right");var subQ1=sQuery(id+"F0.wireOp",EDGE,"E5.top");var subQ2=makeQuery(id+"F0.imprint","INTERSECT",VERTEX,{"derivedFrom":[subQ1,subQ0]});Q57=makeQuery(id+"F0.imprint","IMPRINT",FACE,{"disambiguationData":[TD([[makeQuery(id+"F0.imprint","IMPRINT",EDGE,{"disambiguationData":[TD([[subQ2,1.0]])],"derivedFrom":subQ1}),-1.0]])]});}
            var Q58;
            {var subQ0=sQuery(id+"F0.wireOp",EDGE,"E5.left");var subQ1=sQuery(id+"F0.wireOp",EDGE,"E5.top");var subQ2=makeQuery(id+"F0.imprint","INTERSECT",VERTEX,{"derivedFrom":[subQ1,subQ0]});Q58=makeQuery(id+"F0.imprint","IMPRINT",FACE,{"disambiguationData":[TD([[makeQuery(id+"F0.imprint","IMPRINT",EDGE,{"disambiguationData":[TD([[subQ2,-1.0]])],"derivedFrom":subQ1}),-1.0]])]});}
            var Q59;
            {var subQ0=sQuery(id+"F0.wireOp",EDGE,"E7.MirrorCS");var subQ1=sQuery(id+"F0.wireOp",EDGE,"E6.MirrorCS");var subQ2=makeQuery(id+"F0.imprint","INTERSECT",VERTEX,{"derivedFrom":[subQ1,subQ0]});Q59=makeQuery(id+"F0.imprint","IMPRINT",FACE,{"disambiguationData":[TD([[makeQuery(id+"F0.imprint","IMPRINT",EDGE,{"disambiguationData":[TD([[subQ2,-1.0]])],"derivedFrom":subQ1}),-1.0]])]});}
            var Q60;
            {var subQ0=sQuery(id+"F0.wireOp",EDGE,"E8.MirrorCS");var subQ1=sQuery(id+"F0.wireOp",EDGE,"E7.MirrorCS");var subQ2=makeQuery(id+"F0.imprint","INTERSECT",VERTEX,{"derivedFrom":[subQ1,subQ0]});Q60=makeQuery(id+"F0.imprint","IMPRINT",FACE,{"disambiguationData":[TD([[makeQuery(id+"F0.imprint","IMPRINT",EDGE,{"disambiguationData":[TD([[subQ2,-1.0]])],"derivedFrom":subQ1}),-1.0]])]});}
            var Q61;
            {var subQ0=sQuery(id+"F0.wireOp",EDGE,"E9.MirrorCS");var subQ1=sQuery(id+"F0.wireOp",EDGE,"E8.MirrorCS");var subQ2=makeQuery(id+"F0.imprint","INTERSECT",VERTEX,{"derivedFrom":[subQ1,subQ0]});Q61=makeQuery(id+"F0.imprint","IMPRINT",FACE,{"disambiguationData":[TD([[makeQuery(id+"F0.imprint","IMPRINT",EDGE,{"disambiguationData":[TD([[subQ2,1.0]])],"derivedFrom":subQ1}),1.0]])]});}
            var Q62;
            {var subQ0=sQuery(id+"F0.wireOp",EDGE,"E9.MirrorCS");var subQ1=sQuery(id+"F0.wireOp",EDGE,"E6.MirrorCS");var subQ2=makeQuery(id+"F0.imprint","INTERSECT",VERTEX,{"derivedFrom":[subQ1,subQ0]});Q62=makeQuery(id+"F0.imprint","IMPRINT",FACE,{"disambiguationData":[TD([[makeQuery(id+"F0.imprint","IMPRINT",EDGE,{"disambiguationData":[TD([[subQ2,1.0]])],"derivedFrom":subQ1}),-1.0]])]});}
            var Q63;
            {var subQ0=sQuery(id+"F0.wireOp",EDGE,"E37.MirrorCS");var subQ1=sQuery(id+"F0.wireOp",EDGE,"E36.MirrorCS");var subQ2=makeQuery(id+"F0.imprint","INTERSECT",VERTEX,{"derivedFrom":[subQ1,subQ0]});Q63=makeQuery(id+"F0.imprint","IMPRINT",FACE,{"disambiguationData":[TD([[makeQuery(id+"F0.imprint","IMPRINT",EDGE,{"disambiguationData":[TD([[subQ2,-1.0]])],"derivedFrom":subQ1}),-1.0]])]});}
            var Q64;
            {var subQ0=sQuery(id+"F0.wireOp",EDGE,"E37.MirrorCS");var subQ1=sQuery(id+"F0.wireOp",EDGE,"E34.MirrorCS");var subQ2=makeQuery(id+"F0.imprint","INTERSECT",VERTEX,{"derivedFrom":[subQ1,subQ0]});Q64=makeQuery(id+"F0.imprint","IMPRINT",FACE,{"disambiguationData":[TD([[makeQuery(id+"F0.imprint","IMPRINT",EDGE,{"disambiguationData":[TD([[subQ2,-1.0]])],"derivedFrom":subQ1}),1.0]])]});}
            var Q65;
            {var subQ0=sQuery(id+"F0.wireOp",EDGE,"E38.MirrorCS");var subQ1=sQuery(id+"F0.wireOp",EDGE,"E34.MirrorCS");var subQ2=makeQuery(id+"F0.imprint","INTERSECT",VERTEX,{"derivedFrom":[subQ1,subQ0]});Q65=makeQuery(id+"F0.imprint","IMPRINT",FACE,{"disambiguationData":[TD([[makeQuery(id+"F0.imprint","IMPRINT",EDGE,{"disambiguationData":[TD([[subQ2,1.0]])],"derivedFrom":subQ1}),1.0]])]});}
            var Q66;
            {var subQ0=sQuery(id+"F0.wireOp",EDGE,"E38.MirrorCS");var subQ1=sQuery(id+"F0.wireOp",EDGE,"E36.MirrorCS");var subQ2=makeQuery(id+"F0.imprint","INTERSECT",VERTEX,{"derivedFrom":[subQ1,subQ0]});Q66=makeQuery(id+"F0.imprint","IMPRINT",FACE,{"disambiguationData":[TD([[makeQuery(id+"F0.imprint","IMPRINT",EDGE,{"disambiguationData":[TD([[subQ2,1.0]])],"derivedFrom":subQ1}),-1.0]])]});}
            var Q67;
            {var subQ0=sQuery(id+"F0.wireOp",EDGE,"E42.MirrorCS");var subQ1=sQuery(id+"F0.wireOp",EDGE,"E40.MirrorCS");var subQ2=makeQuery(id+"F0.imprint","INTERSECT",VERTEX,{"derivedFrom":[subQ1,subQ0]});Q67=makeQuery(id+"F0.imprint","IMPRINT",FACE,{"disambiguationData":[TD([[makeQuery(id+"F0.imprint","IMPRINT",EDGE,{"disambiguationData":[TD([[subQ2,-1.0]])],"derivedFrom":subQ1}),-1.0]])]});}
            var Q68;
            {var subQ0=sQuery(id+"F0.wireOp",EDGE,"E42.MirrorCS");var subQ1=sQuery(id+"F0.wireOp",EDGE,"E41.MirrorCS");var subQ2=makeQuery(id+"F0.imprint","INTERSECT",VERTEX,{"derivedFrom":[subQ1,subQ0]});Q68=makeQuery(id+"F0.imprint","IMPRINT",FACE,{"disambiguationData":[TD([[makeQuery(id+"F0.imprint","IMPRINT",EDGE,{"disambiguationData":[TD([[subQ2,-1.0]])],"derivedFrom":subQ1}),1.0]])]});}
            var Q69;
            {var subQ0=sQuery(id+"F0.wireOp",EDGE,"E41.MirrorCS");var subQ1=sQuery(id+"F0.wireOp",EDGE,"E39.MirrorCS");var subQ2=makeQuery(id+"F0.imprint","INTERSECT",VERTEX,{"derivedFrom":[subQ1,subQ0]});Q69=makeQuery(id+"F0.imprint","IMPRINT",FACE,{"disambiguationData":[TD([[makeQuery(id+"F0.imprint","IMPRINT",EDGE,{"disambiguationData":[TD([[subQ2,-1.0]])],"derivedFrom":subQ1}),1.0]])]});}
            var Q70;
            {var subQ0=sQuery(id+"F0.wireOp",EDGE,"E40.MirrorCS");var subQ1=sQuery(id+"F0.wireOp",EDGE,"E39.MirrorCS");var subQ2=makeQuery(id+"F0.imprint","INTERSECT",VERTEX,{"derivedFrom":[subQ1,subQ0]});Q70=makeQuery(id+"F0.imprint","IMPRINT",FACE,{"disambiguationData":[TD([[makeQuery(id+"F0.imprint","IMPRINT",EDGE,{"disambiguationData":[TD([[subQ2,1.0]])],"derivedFrom":subQ1}),1.0]])]});}
            var Q71;
            {var subQ0=sQuery(id+"F0.wireOp",EDGE,"E59.MirrorCS");var subQ1=sQuery(id+"F0.wireOp",EDGE,"E58.MirrorCS");var subQ2=makeQuery(id+"F0.imprint","INTERSECT",VERTEX,{"derivedFrom":[subQ1,subQ0]});Q71=makeQuery(id+"F0.imprint","IMPRINT",FACE,{"disambiguationData":[TD([[makeQuery(id+"F0.imprint","IMPRINT",EDGE,{"disambiguationData":[TD([[subQ2,-1.0]])],"derivedFrom":subQ1}),1.0]])]});}
            var Q72;
            {var subQ0=sQuery(id+"F0.wireOp",EDGE,"E58.MirrorCS");var subQ1=sQuery(id+"F0.wireOp",EDGE,"E56.MirrorCS");var subQ2=makeQuery(id+"F0.imprint","INTERSECT",VERTEX,{"derivedFrom":[subQ1,subQ0]});Q72=makeQuery(id+"F0.imprint","IMPRINT",FACE,{"disambiguationData":[TD([[makeQuery(id+"F0.imprint","IMPRINT",EDGE,{"disambiguationData":[TD([[subQ2,1.0]])],"derivedFrom":subQ1}),-1.0]])]});}
            var Q73;
            {var subQ0=sQuery(id+"F0.wireOp",EDGE,"E56.MirrorCS");var subQ1=sQuery(id+"F0.wireOp",EDGE,"E55.MirrorCS");var subQ2=makeQuery(id+"F0.imprint","INTERSECT",VERTEX,{"derivedFrom":[subQ1,subQ0]});Q73=makeQuery(id+"F0.imprint","IMPRINT",FACE,{"disambiguationData":[TD([[makeQuery(id+"F0.imprint","IMPRINT",EDGE,{"disambiguationData":[TD([[subQ2,1.0]])],"derivedFrom":subQ1}),-1.0]])]});}
            var Q74;
            {var subQ0=sQuery(id+"F0.wireOp",EDGE,"E59.MirrorCS");var subQ1=sQuery(id+"F0.wireOp",EDGE,"E55.MirrorCS");var subQ2=makeQuery(id+"F0.imprint","INTERSECT",VERTEX,{"derivedFrom":[subQ1,subQ0]});Q74=makeQuery(id+"F0.imprint","IMPRINT",FACE,{"disambiguationData":[TD([[makeQuery(id+"F0.imprint","IMPRINT",EDGE,{"disambiguationData":[TD([[subQ2,-1.0]])],"derivedFrom":subQ1}),-1.0]])]});}
            var Q75;
            {var subQ0=sQuery(id+"F0.wireOp",EDGE,"E64.MirrorCS");var subQ1=sQuery(id+"F0.wireOp",EDGE,"E62.MirrorCS");var subQ2=makeQuery(id+"F0.imprint","INTERSECT",VERTEX,{"derivedFrom":[subQ1,subQ0]});Q75=makeQuery(id+"F0.imprint","IMPRINT",FACE,{"disambiguationData":[TD([[makeQuery(id+"F0.imprint","IMPRINT",EDGE,{"disambiguationData":[TD([[subQ2,1.0]])],"derivedFrom":subQ1}),-1.0]])]});}
            var Q76;
            {var subQ0=sQuery(id+"F0.wireOp",EDGE,"E62.MirrorCS");var subQ1=sQuery(id+"F0.wireOp",EDGE,"E61.MirrorCS");var subQ2=makeQuery(id+"F0.imprint","INTERSECT",VERTEX,{"derivedFrom":[subQ1,subQ0]});Q76=makeQuery(id+"F0.imprint","IMPRINT",FACE,{"disambiguationData":[TD([[makeQuery(id+"F0.imprint","IMPRINT",EDGE,{"disambiguationData":[TD([[subQ2,-1.0]])],"derivedFrom":subQ1}),1.0]])]});}
            var Q77;
            {var subQ0=sQuery(id+"F0.wireOp",EDGE,"E61.MirrorCS");var subQ1=sQuery(id+"F0.wireOp",EDGE,"E60.MirrorCS");var subQ2=makeQuery(id+"F0.imprint","INTERSECT",VERTEX,{"derivedFrom":[subQ1,subQ0]});Q77=makeQuery(id+"F0.imprint","IMPRINT",FACE,{"disambiguationData":[TD([[makeQuery(id+"F0.imprint","IMPRINT",EDGE,{"disambiguationData":[TD([[subQ2,-1.0]])],"derivedFrom":subQ1}),1.0]])]});}
            var Q78;
            {var subQ0=sQuery(id+"F0.wireOp",EDGE,"E64.MirrorCS");var subQ1=sQuery(id+"F0.wireOp",EDGE,"E60.MirrorCS");var subQ2=makeQuery(id+"F0.imprint","INTERSECT",VERTEX,{"derivedFrom":[subQ1,subQ0]});Q78=makeQuery(id+"F0.imprint","IMPRINT",FACE,{"disambiguationData":[TD([[makeQuery(id+"F0.imprint","IMPRINT",EDGE,{"disambiguationData":[TD([[subQ2,1.0]])],"derivedFrom":subQ1}),1.0]])]});}
            extrude(context, id + "F1", {"entities" : qUnion([Q0, Q1, Q2, Q3, Q4, Q5, Q6, Q7, Q8, Q9, Q10, Q11, Q12, Q13, Q14, Q15, Q16, Q17, Q18, Q19, Q20, Q21, Q22, Q23, Q24, Q25, Q26, Q27, Q28, Q29, Q30, Q31, Q32, Q33, Q34, Q35, Q36, Q37, Q38, Q39, Q40, Q41, Q42, Q43, Q44, Q45, Q46, Q47, Q48, Q49, Q50, Q51, Q52, Q53, Q54, Q55, Q56, Q57, Q58, Q59, Q60, Q61, Q62, Q63, Q64, Q65, Q66, Q67, Q68, Q69, Q70, Q71, Q72, Q73, Q74, Q75, Q76, Q77, Q78]), "endBound" : BoundingType.SYMMETRIC, "oppositeDirection" : true, "depth" : 3.17 * mm});
        }
    });
